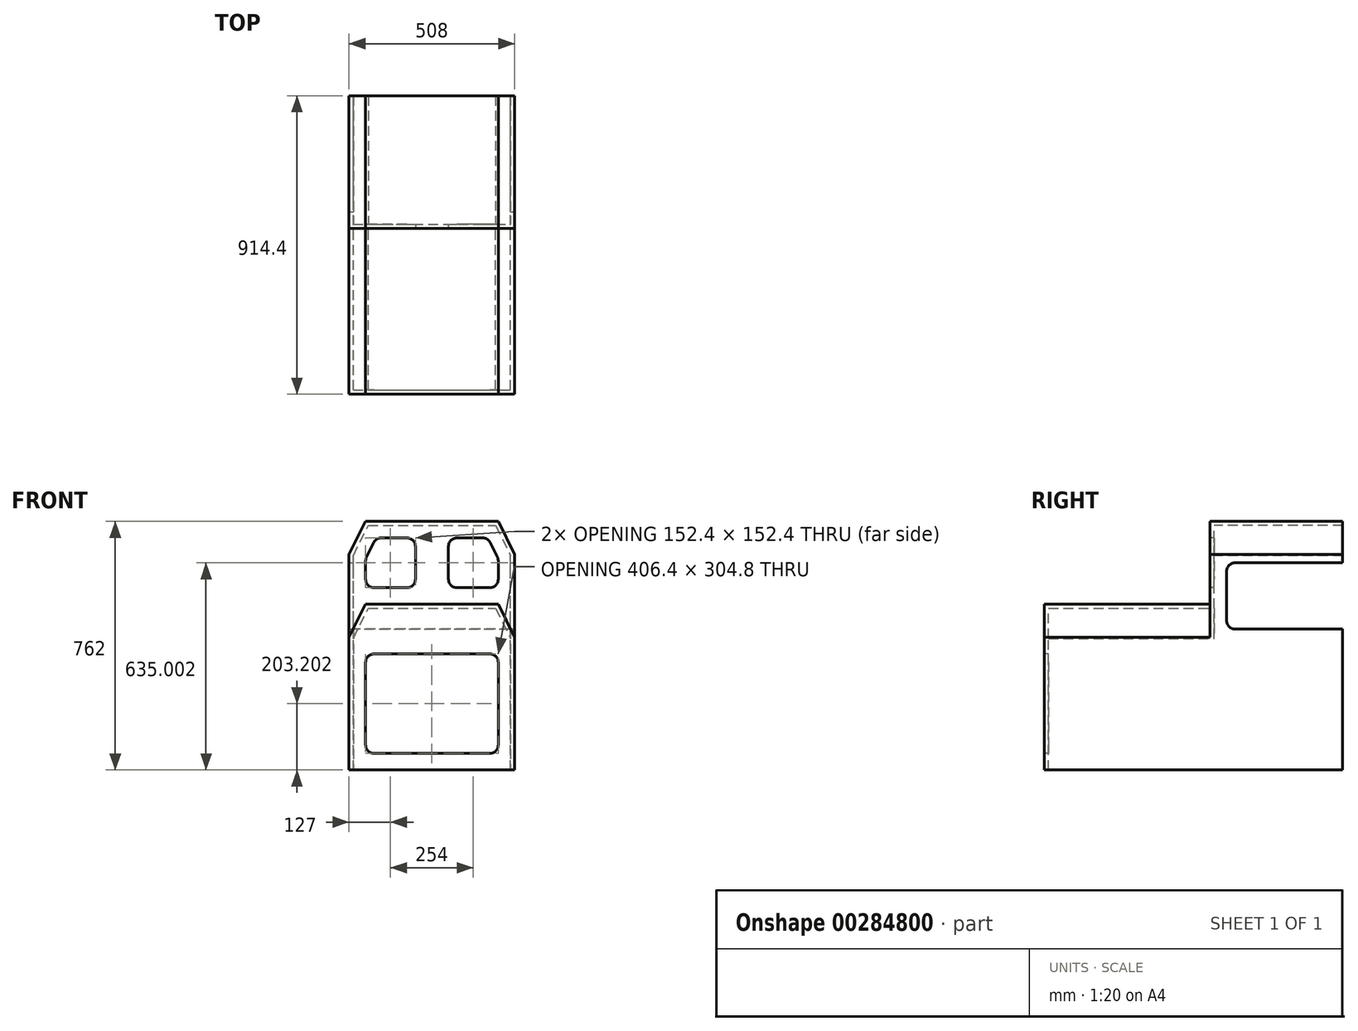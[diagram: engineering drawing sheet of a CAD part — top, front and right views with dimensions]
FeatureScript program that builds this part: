
annotation { "Feature Type Name" : "Feature", "Feature Type Description" : "" }
export const myFeature = defineFeature(function(context is Context, id is Id, definition is map)
    precondition{}
    {
        {
            var Q0;
            Q0=qCreatedBy(makeId("Front.planeOp"),FACE);
            var sketch = newSketch(context, id + "F0", { "sketchPlane" : qUnion([Q0])});
            skLineSegment(sketch, "E0", {"start": v(-228.6, -251.3) * mm, "end": v(279.4, -251.3) * mm});
            skLineSegment(sketch, "E1", {"start": v(279.4, -251.3) * mm, "end": v(279.4, 155.1) * mm});
            skLineSegment(sketch, "E2", {"start": v(-228.6, -251.3) * mm, "end": v(-228.6, 155.1) * mm});
            skPoint(sketch, "E3", {"position": v(0, 256.7) * mm});
            skLineSegment(sketch, "E4", {"start": v(-228.6, 155.1) * mm, "end": v(-177.8, 256.7) * mm});
            skLineSegment(sketch, "E5", {"start": v(-177.8, 256.7) * mm, "end": v(228.6, 256.7) * mm});
            skLineSegment(sketch, "E6", {"start": v(228.6, 256.7) * mm, "end": v(279.4, 155.1) * mm});
            skSolve(sketch);
        }
        {
            var Q0;
            Q0 = qSketchRegion(id + "F0", true);
            extrude(context, id + "F1", {"entities" : qUnion([Q0]), "depth" : 508 * mm});
        }
        {
            var Q0;
            Q0=makeQuery(id+"F1.opExtrude","CAP_FACE",FACE,{"disambiguationData":[OSD([sQuery(id+"F0.wireOp",EDGE,"E0"),sQuery(id+"F0.wireOp",EDGE,"E1"),sQuery(id+"F0.wireOp",EDGE,"E2"),sQuery(id+"F0.wireOp",EDGE,"nImkNcMx-urv2-CTpI-qVrP-bBH4m9cW221N")])],"isStart":true});
            var sketch = newSketch(context, id + "F2", { "sketchPlane" : qUnion([Q0])});
            skLineSegment(sketch, "E7.bottom", {"start": v(-279.4, -251.3) * mm, "end": v(228.6, -251.3) * mm});
            skLineSegment(sketch, "E7.left", {"start": v(-279.4, -251.3) * mm, "end": v(-279.4, 409.1) * mm});
            skLineSegment(sketch, "E7.right", {"start": v(228.6, -251.3) * mm, "end": v(228.6, 409.1) * mm});
            skPoint(sketch, "E8", {"position": v(0, 510.7) * mm});
            skLineSegment(sketch, "E9", {"start": v(228.6, 409.1) * mm, "end": v(177.8, 510.7) * mm});
            skLineSegment(sketch, "E10", {"start": v(177.8, 510.7) * mm, "end": v(-228.6, 510.7) * mm});
            skLineSegment(sketch, "E11", {"start": v(-228.6, 510.7) * mm, "end": v(-279.4, 409.1) * mm});
            skSolve(sketch);
        }
        {
            var Q0;
            Q0 = qSketchRegion(id + "F2", true);
            extrude(context, id + "F3", {"entities" : qUnion([Q0]), "operationType" : NewBodyOperationType.ADD, "depth" : 406.4 * mm});
        }
        {
            var Q0;
            Q0=makeQuery(id+"F3.boolean.opBoolean","MERGE",FACE,{"derivedFrom":[makeQuery(id+"F1.opExtrude","SWEPT_FACE",FACE,{"disambiguationData":[OSD([sQuery(id+"F0.wireOp",EDGE,"E0")])]}),makeQuery(id+"F3.opExtrude","SWEPT_FACE",FACE,{"disambiguationData":[OSD([sQuery(id+"F2.wireOp",EDGE,"E7.bottom")])]})]});
            var Q1;
            Q1=makeQuery(id+"F3.opExtrude","CAP_FACE",FACE,{"disambiguationData":[OSD([sQuery(id+"F2.wireOp",EDGE,"E7.bottom"),sQuery(id+"F2.wireOp",EDGE,"E7.left"),sQuery(id+"F2.wireOp",EDGE,"E7.right"),sQuery(id+"F2.wireOp",EDGE,"rb5KYmV5-Olld-9Bs4-thWg-NdpTlBfu6YXQ")])],"isStart":false});
            shell(context, id + "F4", {"entities" : qUnion([Q0, Q1]), "thickness" : 12.7 * mm});
        }
        {
            var Q0;
            Q0=makeQuery(id+"F3.boolean.opBoolean","MERGE",FACE,{"derivedFrom":[makeQuery(id+"F1.opExtrude","SWEPT_FACE",FACE,{"disambiguationData":[OSD([sQuery(id+"F0.wireOp",EDGE,"E1")])]}),makeQuery(id+"F3.opExtrude","SWEPT_FACE",FACE,{"disambiguationData":[OSD([sQuery(id+"F2.wireOp",EDGE,"E7.left")])]})]});
            var sketch = newSketch(context, id + "F5", { "sketchPlane" : qUnion([Q0])});
            skLineSegment(sketch, "E12.bottom", {"start": v(406.4, 383.7) * mm, "end": v(76.2, 383.7) * mm});
            skLineSegment(sketch, "E12.top", {"start": v(406.4, 180.5) * mm, "end": v(76.2, 180.5) * mm});
            skLineSegment(sketch, "E12.left", {"start": v(406.4, 383.7) * mm, "end": v(406.4, 180.5) * mm});
            skLineSegment(sketch, "E12.right", {"start": v(50.8, 358.3) * mm, "end": v(50.8, 205.9) * mm});
            skPoint(sketch, "E13.visualSharp", {"position": v(50.8, 383.7) * mm});
            skArc(sketch, "E13.filletArc", {"start": v(76.2, 383.7) * mm, "mid": v(58.24, 376.25) * mm, "end": v(50.8, 358.3) * mm});
            skPoint(sketch, "E14.visualSharp", {"position": v(50.8, 180.5) * mm});
            skArc(sketch, "E14.filletArc", {"start": v(50.8, 205.9) * mm, "mid": v(58.24, 187.93) * mm, "end": v(76.2, 180.5) * mm});
            skSolve(sketch);
        }
        {
            var Q0;
            Q0 = qSketchRegion(id + "F5", true);
            extrude(context, id + "F6", {"entities" : qUnion([Q0]), "operationType" : NewBodyOperationType.REMOVE, "endBound" : BoundingType.THROUGH_ALL, "oppositeDirection" : true, "depth" : 25.4 * mm});
        }
        {
            var Q0;
            Q0=makeQuery(id+"F1.opExtrude","CAP_FACE",FACE,{"disambiguationData":[OSD([sQuery(id+"F0.wireOp",EDGE,"E0"),sQuery(id+"F0.wireOp",EDGE,"E1"),sQuery(id+"F0.wireOp",EDGE,"E2"),sQuery(id+"F0.wireOp",EDGE,"nImkNcMx-urv2-CTpI-qVrP-bBH4m9cW221N")])],"isStart":false});
            var sketch = newSketch(context, id + "F7", { "sketchPlane" : qUnion([Q0])});
            skLineSegment(sketch, "E15.bottom", {"start": v(-152.4, 104.3) * mm, "end": v(203.2, 104.3) * mm});
            skLineSegment(sketch, "E15.top", {"start": v(-152.4, -200.5) * mm, "end": v(203.2, -200.5) * mm});
            skLineSegment(sketch, "E15.left", {"start": v(-177.8, 78.9) * mm, "end": v(-177.8, -175.1) * mm});
            skLineSegment(sketch, "E15.right", {"start": v(228.6, 78.9) * mm, "end": v(228.6, -175.1) * mm});
            skPoint(sketch, "E16.visualSharp", {"position": v(-177.8, 104.3) * mm});
            skArc(sketch, "E16.filletArc", {"start": v(-152.4, 104.3) * mm, "mid": v(-170.36, 96.85) * mm, "end": v(-177.8, 78.9) * mm});
            skPoint(sketch, "E17.visualSharp", {"position": v(228.6, 104.3) * mm});
            skArc(sketch, "E17.filletArc", {"start": v(228.6, 78.9) * mm, "mid": v(221.16, 96.85) * mm, "end": v(203.2, 104.3) * mm});
            skPoint(sketch, "E18.visualSharp", {"position": v(228.6, -200.5) * mm});
            skArc(sketch, "E18.filletArc", {"start": v(203.2, -200.5) * mm, "mid": v(221.16, -193.07) * mm, "end": v(228.6, -175.1) * mm});
            skPoint(sketch, "E19.visualSharp", {"position": v(-177.8, -200.5) * mm});
            skArc(sketch, "E19.filletArc", {"start": v(-177.8, -175.1) * mm, "mid": v(-170.36, -193.07) * mm, "end": v(-152.4, -200.5) * mm});
            skSolve(sketch);
        }
        {
            var Q0;
            Q0 = qSketchRegion(id + "F7", true);
            extrude(context, id + "F8", {"entities" : qUnion([Q0]), "operationType" : NewBodyOperationType.REMOVE, "oppositeDirection" : true, "depth" : 25.4 * mm});
        }
        {
            var Q0;
            Q0=makeQuery(id+"F3.opExtrude","CAP_FACE",FACE,{"disambiguationData":[OSD([sQuery(id+"F2.wireOp",EDGE,"E7.bottom"),sQuery(id+"F2.wireOp",EDGE,"E7.left"),sQuery(id+"F2.wireOp",EDGE,"E7.right"),sQuery(id+"F2.wireOp",EDGE,"E9"),sQuery(id+"F2.wireOp",EDGE,"E10"),sQuery(id+"F2.wireOp",EDGE,"E11")])],"isStart":true});
            var sketch = newSketch(context, id + "F9", { "sketchPlane" : qUnion([Q0])});
            skLineSegment(sketch, "E20", {"start": v(-152.4, 307.5) * mm, "end": v(-50.8, 307.5) * mm});
            skLineSegment(sketch, "E21", {"start": v(-25.4, 332.9) * mm, "end": v(-25.4, 434.5) * mm});
            skLineSegment(sketch, "E22", {"start": v(-50.8, 459.9) * mm, "end": v(-130.7, 459.9) * mm});
            skLineSegment(sketch, "E23", {"start": v(-153.42, 445.85) * mm, "end": v(-175.12, 402.46) * mm});
            skLineSegment(sketch, "E24", {"start": v(-177.8, 391.1) * mm, "end": v(-177.8, 332.9) * mm});
            skLineSegment(sketch, "E25", {"start": v(76.2, 434.5) * mm, "end": v(76.2, 332.9) * mm});
            skLineSegment(sketch, "E26", {"start": v(101.6, 307.5) * mm, "end": v(203.2, 307.5) * mm});
            skLineSegment(sketch, "E27", {"start": v(228.6, 332.9) * mm, "end": v(228.6, 391.1) * mm});
            skLineSegment(sketch, "E28", {"start": v(101.6, 459.9) * mm, "end": v(181.5, 459.9) * mm});
            skLineSegment(sketch, "E29", {"start": v(204.22, 445.85) * mm, "end": v(225.92, 402.46) * mm});
            skPoint(sketch, "E30.visualSharp", {"position": v(-177.8, 397.1) * mm});
            skArc(sketch, "E30.filletArc", {"start": v(-175.12, 402.46) * mm, "mid": v(-177.12, 396.94) * mm, "end": v(-177.8, 391.1) * mm});
            skPoint(sketch, "E31.visualSharp", {"position": v(-146.4, 459.9) * mm});
            skArc(sketch, "E31.filletArc", {"start": v(-130.7, 459.9) * mm, "mid": v(-144.06, 456.1) * mm, "end": v(-153.42, 445.85) * mm});
            skPoint(sketch, "E32.visualSharp", {"position": v(-25.4, 459.9) * mm});
            skArc(sketch, "E32.filletArc", {"start": v(-25.4, 434.5) * mm, "mid": v(-32.84, 452.45) * mm, "end": v(-50.8, 459.9) * mm});
            skPoint(sketch, "E33.visualSharp", {"position": v(-25.4, 307.5) * mm});
            skArc(sketch, "E33.filletArc", {"start": v(-50.8, 307.5) * mm, "mid": v(-32.84, 314.93) * mm, "end": v(-25.4, 332.9) * mm});
            skPoint(sketch, "E34.visualSharp", {"position": v(-177.8, 307.5) * mm});
            skArc(sketch, "E34.filletArc", {"start": v(-177.8, 332.9) * mm, "mid": v(-170.36, 314.93) * mm, "end": v(-152.4, 307.5) * mm});
            skPoint(sketch, "E35.visualSharp", {"position": v(76.2, 307.5) * mm});
            skArc(sketch, "E35.filletArc", {"start": v(76.2, 332.9) * mm, "mid": v(83.64, 314.93) * mm, "end": v(101.6, 307.5) * mm});
            skPoint(sketch, "E36.visualSharp", {"position": v(76.2, 459.9) * mm});
            skArc(sketch, "E36.filletArc", {"start": v(101.6, 459.9) * mm, "mid": v(83.64, 452.45) * mm, "end": v(76.2, 434.5) * mm});
            skPoint(sketch, "E37.visualSharp", {"position": v(197.2, 459.9) * mm});
            skArc(sketch, "E37.filletArc", {"start": v(204.22, 445.85) * mm, "mid": v(194.86, 456.1) * mm, "end": v(181.5, 459.9) * mm});
            skPoint(sketch, "E38.visualSharp", {"position": v(228.6, 397.1) * mm});
            skArc(sketch, "E38.filletArc", {"start": v(228.6, 391.1) * mm, "mid": v(227.92, 396.94) * mm, "end": v(225.92, 402.46) * mm});
            skPoint(sketch, "E39.visualSharp", {"position": v(228.6, 307.5) * mm});
            skArc(sketch, "E39.filletArc", {"start": v(203.2, 307.5) * mm, "mid": v(221.16, 314.93) * mm, "end": v(228.6, 332.9) * mm});
            skSolve(sketch);
        }
        {
            var Q0;
            Q0 = qSketchRegion(id + "F9", true);
            extrude(context, id + "F10", {"entities" : qUnion([Q0]), "operationType" : NewBodyOperationType.REMOVE, "oppositeDirection" : true, "depth" : 25.4 * mm});
        }
        {
            var Q0;
            {var subQ0=sQuery(id+"F2.wireOp",EDGE,"E7.left");var subQ1=sQuery(id+"F2.wireOp",EDGE,"E7.bottom");var subQ2=sQuery(id+"F0.wireOp",EDGE,"E1");Q0=makeQuery(id+"F6.boolean.opBoolean","SPLIT",FACE,{"disambiguationData":[TD([makeQuery(id+"F1.opExtrude","SWEPT_FACE",FACE,{"disambiguationData":[OSD([sQuery(id+"F0.wireOp",EDGE,"E0")])]}),makeQuery(id+"F1.opExtrude","SWEPT_FACE",FACE,{"disambiguationData":[OSD([subQ2])]}),makeQuery(id+"F3.opExtrude","SWEPT_FACE",FACE,{"disambiguationData":[OSD([subQ1])]}),makeQuery(id+"F3.opExtrude","SWEPT_FACE",FACE,{"disambiguationData":[OSD([subQ0])]}),makeQuery(id+"F4.opShell","OFFSET_FACE",FACE,{"disambiguationData":[OSD([subQ2,subQ0])]}),makeQuery(id+"F6.opExtrude","SWEPT_FACE",FACE,{"disambiguationData":[OSD([sQuery(id+"F5.wireOp",EDGE,"E12.top")])]})])],"derivedFrom":makeQuery(id+"F3.opExtrude","CAP_FACE",FACE,{"disambiguationData":[OSD([subQ1,subQ0,sQuery(id+"F2.wireOp",EDGE,"E7.right"),sQuery(id+"F2.wireOp",EDGE,"E9"),sQuery(id+"F2.wireOp",EDGE,"E10"),sQuery(id+"F2.wireOp",EDGE,"E11")])],"isStart":false})});}
            var sketch = newSketch(context, id + "F11", { "sketchPlane" : qUnion([Q0])});
            skLineSegment(sketch, "E40.bottom", {"start": v(-279.4, 180.5) * mm, "end": v(228.6, 180.5) * mm});
            skLineSegment(sketch, "E40.top", {"start": v(-279.4, -251.3) * mm, "end": v(228.6, -251.3) * mm});
            skLineSegment(sketch, "E40.left", {"start": v(-279.4, 180.5) * mm, "end": v(-279.4, -251.3) * mm});
            skLineSegment(sketch, "E40.right", {"start": v(228.6, 180.5) * mm, "end": v(228.6, -251.3) * mm});
            skSolve(sketch);
        }
        {
            var Q0;
            Q0 = qSketchRegion(id + "F11", true);
            extrude(context, id + "F12", {"entities" : qUnion([Q0]), "operationType" : NewBodyOperationType.ADD, "oppositeDirection" : true, "depth" : 3 * mm});
        }
    });
